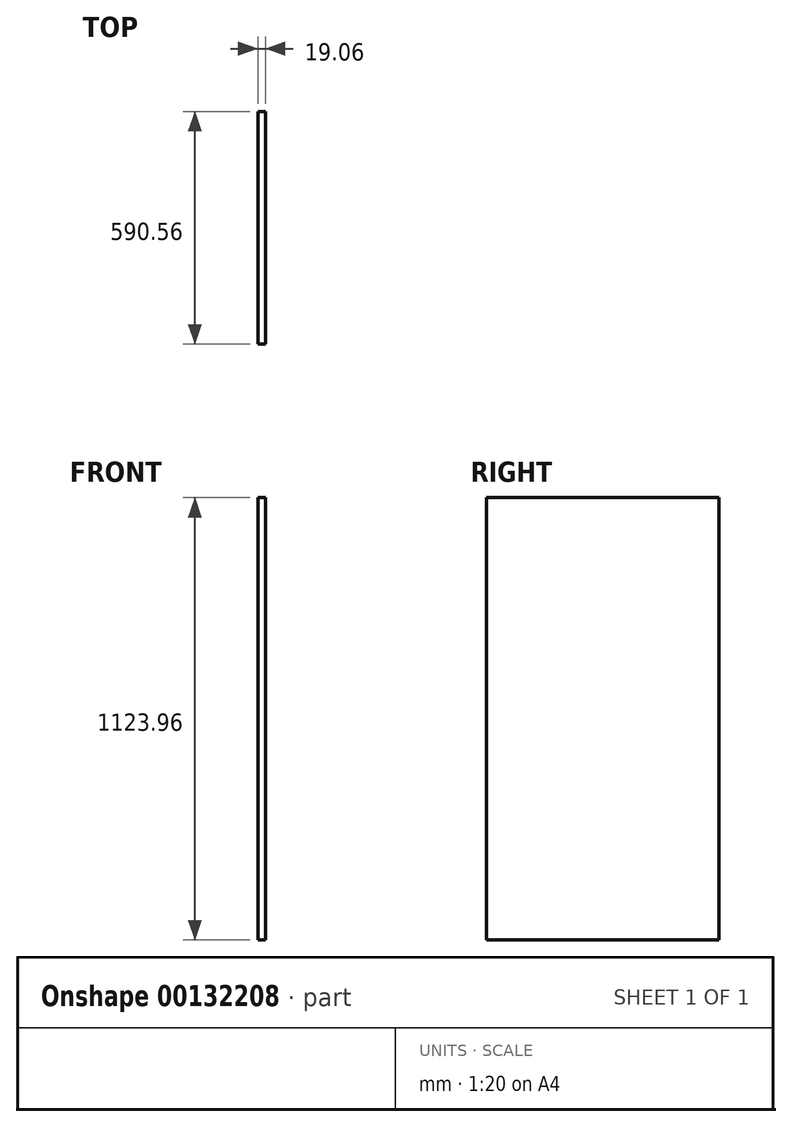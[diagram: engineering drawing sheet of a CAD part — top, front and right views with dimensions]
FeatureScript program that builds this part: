
annotation { "Feature Type Name" : "Feature", "Feature Type Description" : "" }
export const myFeature = defineFeature(function(context is Context, id is Id, definition is map)
    precondition{}
    {
        {
            var Q0;
            Q0=qCreatedBy(makeId("Right.planeOp"),FACE);
            var sketch = newSketch(context, id + "F0", { "sketchPlane" : qUnion([Q0])});
            skLineSegment(sketch, "E0.bottom", {"start": v(295.27, -561.98) * mm, "end": v(-295.28, -561.98) * mm});
            skLineSegment(sketch, "E0.top", {"start": v(295.27, 561.97) * mm, "end": v(-295.28, 561.97) * mm});
            skLineSegment(sketch, "E0.left", {"start": v(295.27, -561.98) * mm, "end": v(295.27, 561.97) * mm});
            skLineSegment(sketch, "E0.right", {"start": v(-295.28, -561.98) * mm, "end": v(-295.28, 561.97) * mm});
            skPoint(sketch, "E0.middle", {"position": v(0, 0) * mm});
            skSolve(sketch);
        }
        {
            var Q0;
            Q0=makeQuery(id+"F0.imprint","IMPRINT",FACE,{"disambiguationData":[TD([[makeQuery(id+"F0.imprint","IMPRINT",EDGE,{"derivedFrom":sQuery(id+"F0.wireOp",EDGE,"E0.bottom")}),-1.0]])]});
            extrude(context, id + "F1", {"entities" : qUnion([Q0]), "endBound" : BoundingType.SYMMETRIC, "depth" : 19.05 * mm});
        }
    });
